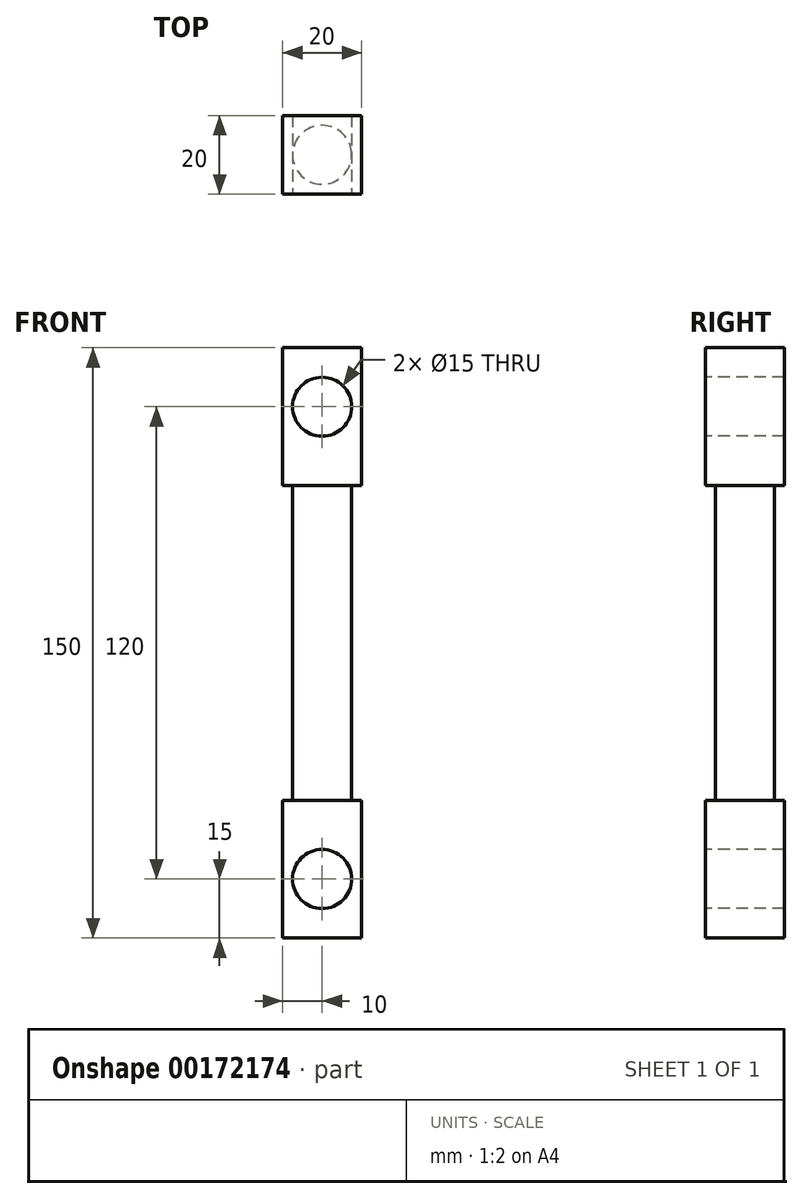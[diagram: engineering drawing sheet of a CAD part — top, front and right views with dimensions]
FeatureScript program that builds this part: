
annotation { "Feature Type Name" : "Feature", "Feature Type Description" : "" }
export const myFeature = defineFeature(function(context is Context, id is Id, definition is map)
    precondition{}
    {
        {
            var Q0;
            Q0=qCreatedBy(makeId("Top.planeOp"),FACE);
            var sketch = newSketch(context, id + "F0", { "sketchPlane" : qUnion([Q0])});
            skCircle(sketch, "E0", {"center": v(0, 0) * mm, "radius": 7.5 * mm});
            skSolve(sketch);
        }
        {
            var Q0;
            Q0=qSketchRegion(id+"F0",true);
            extrude(context, id + "F1", {"entities" : qUnion([Q0]), "depth" : 150 * mm});
        }
        {
            var Q0;
            Q0=qCreatedBy(makeId("Top.planeOp"),FACE);
            cPlane(context, id + "F2", {"entities" : qUnion([Q0]), "cplaneType" : CPlaneType.OFFSET, "offset" : 35 * mm, "width" : 150 * mm, "height" : 150 * mm});
        }
        {
            var Q0;
            Q0=qCreatedBy(makeId("Top.planeOp"),FACE);
            cPlane(context, id + "F3", {"entities" : qUnion([Q0]), "cplaneType" : CPlaneType.OFFSET, "offset" : 115 * mm, "width" : 150 * mm, "height" : 150 * mm});
        }
        {
            var Q0;
            Q0=qCreatedBy(id+"F2.planeOp",FACE);
            var sketch = newSketch(context, id + "F4", { "sketchPlane" : qUnion([Q0])});
            skLineSegment(sketch, "E1.bottom", {"start": v(10, -10) * mm, "end": v(-10, -10) * mm});
            skLineSegment(sketch, "E1.top", {"start": v(10, 10) * mm, "end": v(-10, 10) * mm});
            skLineSegment(sketch, "E1.left", {"start": v(10, -10) * mm, "end": v(10, 10) * mm});
            skLineSegment(sketch, "E1.right", {"start": v(-10, -10) * mm, "end": v(-10, 10) * mm});
            skPoint(sketch, "E1.middle", {"position": v(0, 0) * mm});
            skSolve(sketch);
        }
        {
            var Q0;
            Q0=qSketchRegion(id+"F4",true);
            extrude(context, id + "F5", {"entities" : qUnion([Q0]), "operationType" : NewBodyOperationType.ADD, "oppositeDirection" : true, "depth" : 35 * mm});
        }
        {
            var Q0;
            Q0=qCreatedBy(id+"F3.planeOp",FACE);
            var sketch = newSketch(context, id + "F6", { "sketchPlane" : qUnion([Q0])});
            skLineSegment(sketch, "E2.bottom", {"start": v(10, -10) * mm, "end": v(-10, -10) * mm});
            skLineSegment(sketch, "E2.top", {"start": v(10, 10) * mm, "end": v(-10, 10) * mm});
            skLineSegment(sketch, "E2.left", {"start": v(10, -10) * mm, "end": v(10, 10) * mm});
            skLineSegment(sketch, "E2.right", {"start": v(-10, -10) * mm, "end": v(-10, 10) * mm});
            skPoint(sketch, "E2.middle", {"position": v(0, 0) * mm});
            skSolve(sketch);
        }
        {
            var Q0;
            Q0=qSketchRegion(id+"F6",true);
            extrude(context, id + "F7", {"entities" : qUnion([Q0]), "operationType" : NewBodyOperationType.ADD, "depth" : 35 * mm});
        }
        {
            var Q0;
            Q0=makeQuery(id+"F7.opExtrude","SWEPT_FACE",FACE,{"disambiguationData":[OSD([sQuery(id+"F6.wireOp",EDGE,"E2.bottom")])]});
            var sketch = newSketch(context, id + "F8", { "sketchPlane" : qUnion([Q0])});
            skCircle(sketch, "E3", {"center": v(0, 135) * mm, "radius": 7.5 * mm});
            skCircle(sketch, "E4", {"center": v(0, 15) * mm, "radius": 7.5 * mm});
            skSolve(sketch);
        }
        {
            var Q0;
            Q0 = qSketchRegion(id + "F8", true);
            extrude(context, id + "F9", {"entities" : qUnion([Q0]), "operationType" : NewBodyOperationType.REMOVE, "endBound" : BoundingType.UP_TO_NEXT, "oppositeDirection" : true, "depth" : 25 * mm});
        }
    });
